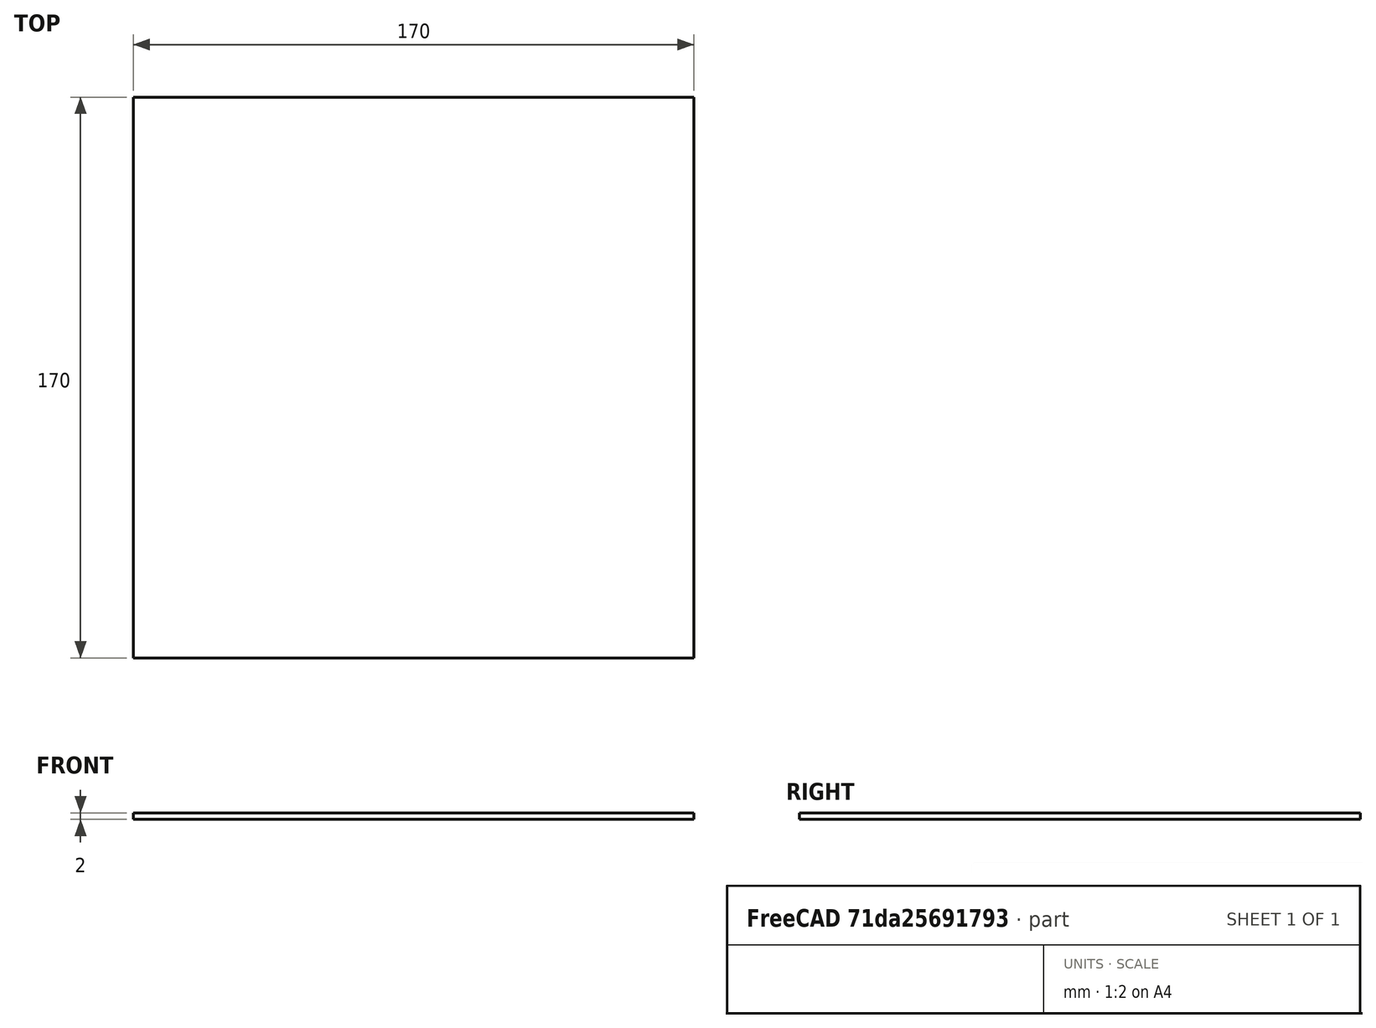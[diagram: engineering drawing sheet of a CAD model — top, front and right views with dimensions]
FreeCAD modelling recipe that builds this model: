
FCSTD DOCUMENT  (FreeCAD 0.18R16131 (Git))
Label: platform
License: All rights reserved
LicenseURL: http://en.wikipedia.org/wiki/All_rights_reserved
objects: Sketcher::SketchObject×1, PartDesign::Pad×1, PartDesign::Body×1
note: 4 computed .brp shape members not serialized (recipe doc carries the construction recipe); baked Part::Feature solids carry a one-line shape summary decoded from their .brp

FEATURE [Sketcher::SketchObject] Sketch
  MapMode = 5
  Support = -> [XY_Plane]
  sketch-geometry (4):
    g0: LineSegment StartX=-71.8771 StartY=-10.4337 StartZ=0 EndX=98.1229 EndY=-10.4337 EndZ=0
    g1: LineSegment StartX=98.1229 StartY=-10.4337 StartZ=0 EndX=98.1229 EndY=159.566 EndZ=0
    g2: LineSegment StartX=98.1229 StartY=159.566 StartZ=0 EndX=-71.8771 EndY=159.566 EndZ=0
    g3: LineSegment StartX=-71.8771 StartY=159.566 StartZ=0 EndX=-71.8771 EndY=-10.4337 EndZ=0
  constraints (10):
    c: Coincident(g0,g1)
    c: Coincident(g1,g2)
    c: Coincident(g2,g3)
    c: Coincident(g3,g0)
    c: Horizontal(g0)
    c: Horizontal(g2)
    c: Vertical(g1)
    c: Vertical(g3)
    c: DistanceX(g0,g0) = 170
    c: DistanceY(g3,g3) = 170
FEATURE [PartDesign::Pad] Pad
  Length = 2
  Length2 = 100
  Profile = -> Sketch
  Type = 0
FEATURE [PartDesign::Body] Body
  Group = -> [Sketch,Pad]
  Origin = -> Origin
  Tip = -> Pad
